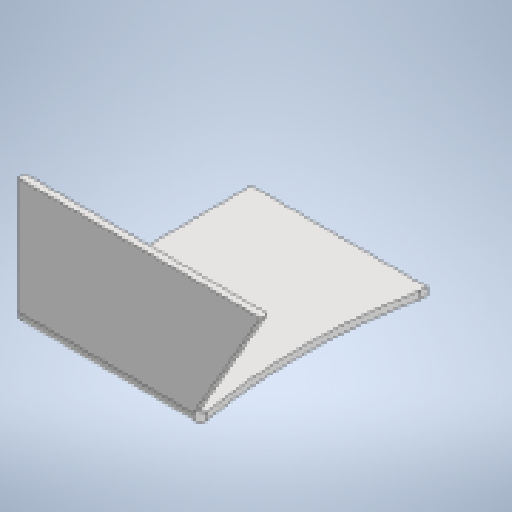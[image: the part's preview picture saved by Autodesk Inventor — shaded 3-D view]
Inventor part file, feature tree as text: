
AUTODESK INVENTOR PART (.ipt)
format: ipt  version: 2025.4 (Build 294407000, 407)  size: 208,896 bytes
history: native  units: mm
features: sheet_metal_op x6, other x4, sketch x3, projected_geometry x1
ambient origin geometry x8: Origin, YZ Plane, XZ Plane, XY Plane, X Axis, Y Axis, Z Axis, Center Point
bodies: Body1 (feature_tree)
feature tree (14):
  sheet_metal_op  "Face2"
  sheet_metal_op  "Flange1"
  sheet_metal_op  "Face3"
  sketch  "Sketch2"  dims[d14=6.0mm]
  other  "Plate2"
  sketch  "Sketch5"  dims[d29=145.0mm]
  other  "Plate3"
  sheet_metal_op  "Bend1"
  sheet_metal_op  "Corner1"
  sketch  "Sketch6"  dims[d30=195.0mm d31=5.0mm d32=5.0mm d33=480.0mm d34=6.0mm d35=3.0mm d36=12.0mm d37=6.0mm d38=110.0mm d39=90.0deg d40=6.0mm d41=24.0mm d42=6.0mm d43=6.0mm d44=30.0deg d47=6.0mm d48=6.0mm d49=3.0mm d50=12.0mm d51=6.0mm]
  projected_geometry  "Projected Loop1"
  other  "Plate4"
  sheet_metal_op  "Bend2"
  other  "Definition1"
